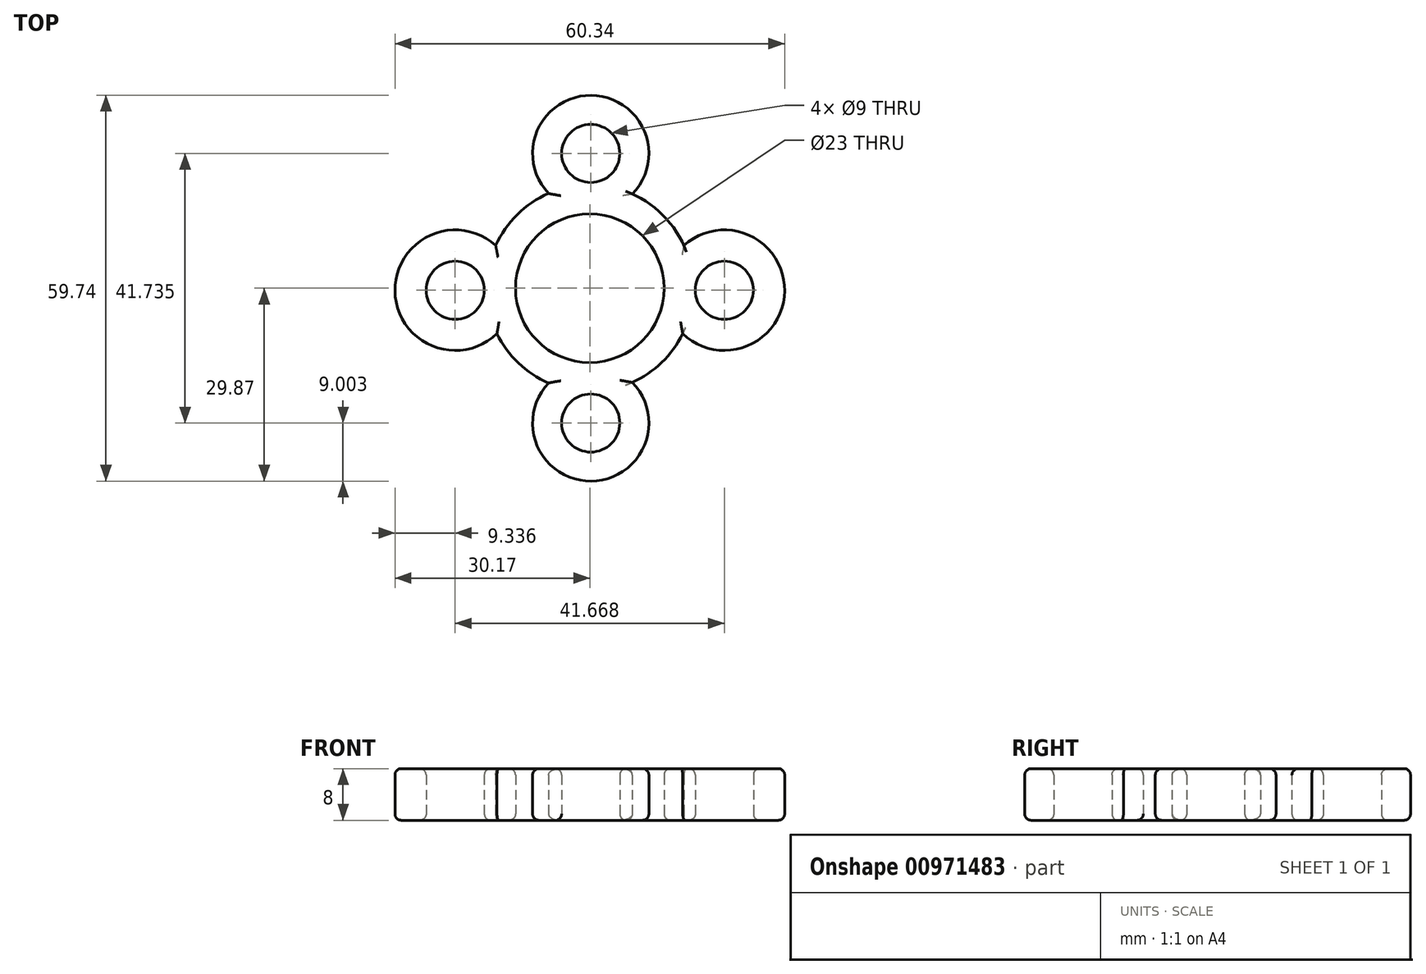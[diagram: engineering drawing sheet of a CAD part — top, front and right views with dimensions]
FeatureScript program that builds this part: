
annotation { "Feature Type Name" : "Feature", "Feature Type Description" : "" }
export const myFeature = defineFeature(function(context is Context, id is Id, definition is map)
    precondition{}
    {
        {
            var Q0;
            Q0=qCreatedBy(makeId("Top.planeOp"),FACE);
            var sketch = newSketch(context, id + "F0", { "sketchPlane" : qUnion([Q0])});
            skArc(sketch, "E0", {"start": v(-14.37, -7.04) * mm, "mid": v(-11.05, -11.57) * mm, "end": v(-6.38, -14.67) * mm});
            skArc(sketch, "E1.MirrorC", {"start": v(14.57, 6.62) * mm, "mid": v(30.17, -0.44) * mm, "end": v(14.37, -7.04) * mm});
            skCircle(sketch, "E2.MirrorC", {"center": v(20.83, -0.3) * mm, "radius": 4.5 * mm});
            skCircle(sketch, "E3.MirrorC", {"center": v(-20.83, -0.3) * mm, "radius": 4.5 * mm});
            skArc(sketch, "E4.MirrorC", {"start": v(-14.57, 6.62) * mm, "mid": v(-30.17, -0.44) * mm, "end": v(-14.37, -7.04) * mm});
            skCircle(sketch, "E5.MirrorC", {"center": v(0.15, 20.87) * mm, "radius": 4.5 * mm});
            skArc(sketch, "E6.MirrorC", {"start": v(6.59, 14.58) * mm, "mid": v(0.2, 29.87) * mm, "end": v(-6.38, 14.67) * mm});
            skArc(sketch, "E7.MirrorC", {"start": v(6.59, -14.58) * mm, "mid": v(0.2, -29.87) * mm, "end": v(-6.38, -14.67) * mm});
            skCircle(sketch, "E8.MirrorC", {"center": v(0.15, -20.87) * mm, "radius": 4.5 * mm});
            skArc(sketch, "E9.trimOffspring", {"start": v(-6.38, 14.67) * mm, "mid": v(-11.22, 11.4) * mm, "end": v(-14.57, 6.62) * mm});
            skArc(sketch, "E10.trimOffspring", {"start": v(14.57, 6.62) * mm, "mid": v(11.3, 11.33) * mm, "end": v(6.59, 14.58) * mm});
            skArc(sketch, "E11.trimOffspring", {"start": v(6.59, -14.58) * mm, "mid": v(11.14, -11.49) * mm, "end": v(14.37, -7.04) * mm});
            skCircle(sketch, "E12", {"center": v(0, 0) * mm, "radius": 11.5 * mm});
            skSolve(sketch);
        }
        {
            var Q0;
            Q0=makeQuery(id+"F0.imprint","IMPRINT",FACE,{"disambiguationData":[TD([[makeQuery(id+"F0.imprint","IMPRINT",EDGE,{"derivedFrom":sQuery(id+"F0.wireOp",EDGE,"E0")}),1.0]])]});
            extrude(context, id + "F1", {"entities" : qUnion([Q0]), "depth" : 8 * mm, "offsetDistance" : 25 * mm});
        }
        {
            var Q0;
            Q0=makeQuery(id+"F1.opExtrude","CAP_EDGE",EDGE,{"disambiguationData":[OSD([sQuery(id+"F0.wireOp",EDGE,"E12")])],"isStart":false});
            var Q1;
            Q1=makeQuery(id+"F1.opExtrude","CAP_EDGE",EDGE,{"disambiguationData":[OSD([sQuery(id+"F0.wireOp",EDGE,"E4.MirrorC")])],"isStart":false});
            var Q2;
            Q2=makeQuery(id+"F1.opExtrude","CAP_EDGE",EDGE,{"disambiguationData":[OSD([sQuery(id+"F0.wireOp",EDGE,"E0")])],"isStart":false});
            var Q3;
            Q3=makeQuery(id+"F1.opExtrude","CAP_EDGE",EDGE,{"disambiguationData":[OSD([sQuery(id+"F0.wireOp",EDGE,"E7.MirrorC")])],"isStart":false});
            var Q4;
            Q4=makeQuery(id+"F1.opExtrude","CAP_EDGE",EDGE,{"disambiguationData":[OSD([sQuery(id+"F0.wireOp",EDGE,"E11.trimOffspring")])],"isStart":false});
            var Q5;
            Q5=makeQuery(id+"F1.opExtrude","CAP_EDGE",EDGE,{"disambiguationData":[OSD([sQuery(id+"F0.wireOp",EDGE,"E1.MirrorC")])],"isStart":false});
            var Q6;
            Q6=makeQuery(id+"F1.opExtrude","CAP_EDGE",EDGE,{"disambiguationData":[OSD([sQuery(id+"F0.wireOp",EDGE,"E6.MirrorC")])],"isStart":false});
            var Q7;
            Q7=makeQuery(id+"F1.opExtrude","CAP_EDGE",EDGE,{"disambiguationData":[OSD([sQuery(id+"F0.wireOp",EDGE,"E9.trimOffspring")])],"isStart":false});
            var Q8;
            Q8=makeQuery(id+"F1.opExtrude","CAP_EDGE",EDGE,{"disambiguationData":[OSD([sQuery(id+"F0.wireOp",EDGE,"E3.MirrorC")])],"isStart":false});
            var Q9;
            Q9=makeQuery(id+"F1.opExtrude","CAP_EDGE",EDGE,{"disambiguationData":[OSD([sQuery(id+"F0.wireOp",EDGE,"E5.MirrorC")])],"isStart":false});
            var Q10;
            Q10=makeQuery(id+"F1.opExtrude","CAP_EDGE",EDGE,{"disambiguationData":[OSD([sQuery(id+"F0.wireOp",EDGE,"E2.MirrorC")])],"isStart":false});
            var Q11;
            Q11=makeQuery(id+"F1.opExtrude","CAP_EDGE",EDGE,{"disambiguationData":[OSD([sQuery(id+"F0.wireOp",EDGE,"E8.MirrorC")])],"isStart":false});
            var Q12;
            Q12=makeQuery(id+"F1.opExtrude","CAP_EDGE",EDGE,{"disambiguationData":[OSD([sQuery(id+"F0.wireOp",EDGE,"E8.MirrorC")])],"isStart":true});
            var Q13;
            Q13=makeQuery(id+"F1.opExtrude","CAP_EDGE",EDGE,{"disambiguationData":[OSD([sQuery(id+"F0.wireOp",EDGE,"E2.MirrorC")])],"isStart":true});
            var Q14;
            Q14=makeQuery(id+"F1.opExtrude","CAP_EDGE",EDGE,{"disambiguationData":[OSD([sQuery(id+"F0.wireOp",EDGE,"E5.MirrorC")])],"isStart":true});
            var Q15;
            Q15=makeQuery(id+"F1.opExtrude","CAP_EDGE",EDGE,{"disambiguationData":[OSD([sQuery(id+"F0.wireOp",EDGE,"E3.MirrorC")])],"isStart":true});
            var Q16;
            Q16=makeQuery(id+"F1.opExtrude","CAP_EDGE",EDGE,{"disambiguationData":[OSD([sQuery(id+"F0.wireOp",EDGE,"E4.MirrorC")])],"isStart":true});
            var Q17;
            Q17=makeQuery(id+"F1.opExtrude","CAP_EDGE",EDGE,{"disambiguationData":[OSD([sQuery(id+"F0.wireOp",EDGE,"E0")])],"isStart":true});
            var Q18;
            Q18=makeQuery(id+"F1.opExtrude","CAP_EDGE",EDGE,{"disambiguationData":[OSD([sQuery(id+"F0.wireOp",EDGE,"E7.MirrorC")])],"isStart":true});
            var Q19;
            Q19=makeQuery(id+"F1.opExtrude","CAP_EDGE",EDGE,{"disambiguationData":[OSD([sQuery(id+"F0.wireOp",EDGE,"E1.MirrorC")])],"isStart":true});
            var Q20;
            Q20=makeQuery(id+"F1.opExtrude","CAP_EDGE",EDGE,{"disambiguationData":[OSD([sQuery(id+"F0.wireOp",EDGE,"E10.trimOffspring")])],"isStart":true});
            var Q21;
            Q21=makeQuery(id+"F1.opExtrude","CAP_EDGE",EDGE,{"disambiguationData":[OSD([sQuery(id+"F0.wireOp",EDGE,"E6.MirrorC")])],"isStart":true});
            var Q22;
            Q22=makeQuery(id+"F1.opExtrude","CAP_EDGE",EDGE,{"disambiguationData":[OSD([sQuery(id+"F0.wireOp",EDGE,"E9.trimOffspring")])],"isStart":true});
            var Q23;
            Q23=makeQuery(id+"F1.opExtrude","CAP_EDGE",EDGE,{"disambiguationData":[OSD([sQuery(id+"F0.wireOp",EDGE,"E12")])],"isStart":true});
            fillet(context, id + "F2", {"entities" : qUnion([Q0, Q1, Q2, Q3, Q4, Q5, Q6, Q7, Q8, Q9, Q10, Q11, Q12, Q13, Q14, Q15, Q16, Q17, Q18, Q19, Q20, Q21, Q22, Q23]), "radius" : 1 * mm, "tangentPropagation" : true, "allowEdgeOverflow" : false});
        }
    });
